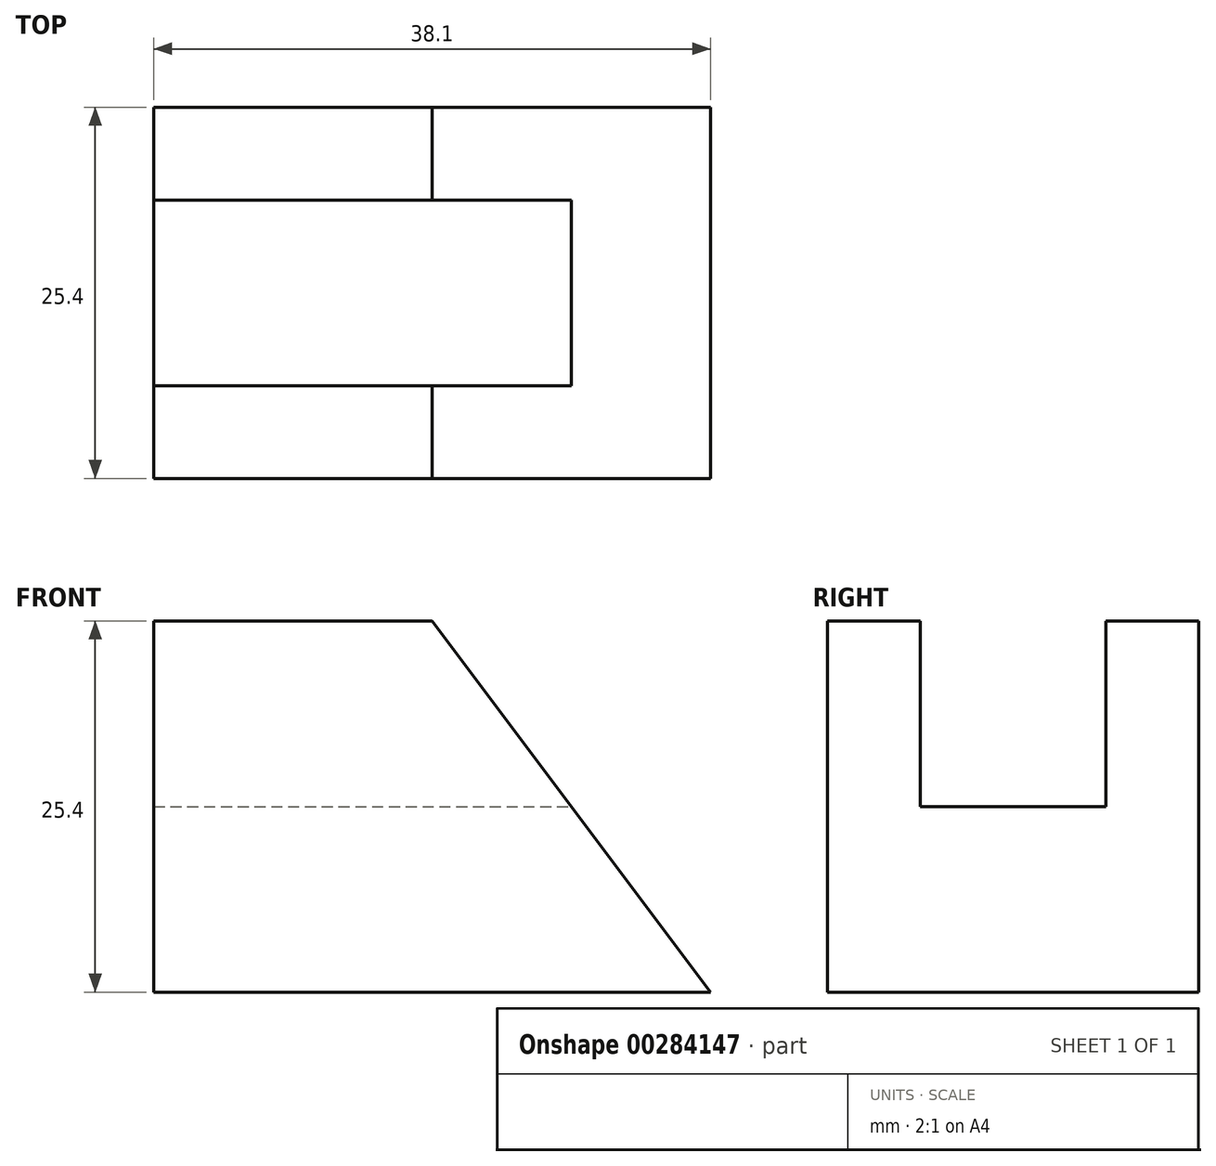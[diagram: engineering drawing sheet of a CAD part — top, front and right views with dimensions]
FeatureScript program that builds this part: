
annotation { "Feature Type Name" : "Feature", "Feature Type Description" : "" }
export const myFeature = defineFeature(function(context is Context, id is Id, definition is map)
    precondition{}
    {
        {
            var Q0;
            Q0=qCreatedBy(makeId("Front.planeOp"),FACE);
            var sketch = newSketch(context, id + "F0", { "sketchPlane" : qUnion([Q0])});
            skLineSegment(sketch, "E0.top", {"start": v(19.05, -12.7) * mm, "end": v(-19.05, -12.7) * mm});
            skLineSegment(sketch, "E0.right", {"start": v(-19.05, 12.7) * mm, "end": v(-19.05, -12.7) * mm});
            skPoint(sketch, "E0.middle", {"position": v(0, 0) * mm});
            skLineSegment(sketch, "E1", {"start": v(-19.05, 12.7) * mm, "end": v(0, 12.7) * mm});
            skLineSegment(sketch, "E2", {"start": v(0, 12.7) * mm, "end": v(19.05, -12.7) * mm});
            skSolve(sketch);
        }
        {
            var Q0;
            Q0=makeQuery(id+"F0.imprint","IMPRINT",FACE,{"disambiguationData":[TD([[makeQuery(id+"F0.imprint","IMPRINT",EDGE,{"derivedFrom":sQuery(id+"F0.wireOp",EDGE,"E0.top")}),-1.0]])]});
            extrude(context, id + "F1", {"entities" : qUnion([Q0]), "endBound" : BoundingType.SYMMETRIC, "depth" : 25.4 * mm});
        }
        {
            var Q0;
            Q0=qCreatedBy(makeId("Right.planeOp"),FACE);
            var sketch = newSketch(context, id + "F2", { "sketchPlane" : qUnion([Q0])});
            skLineSegment(sketch, "E3", {"start": v(-6.35, 0) * mm, "end": v(6.35, 0) * mm});
            skLineSegment(sketch, "E4", {"start": v(6.35, 0) * mm, "end": v(6.35, 12.7) * mm});
            skLineSegment(sketch, "E5", {"start": v(6.35, 12.7) * mm, "end": v(-6.35, 12.7) * mm});
            skLineSegment(sketch, "E6", {"start": v(-6.35, 12.7) * mm, "end": v(-6.35, 0) * mm});
            skSolve(sketch);
        }
        {
            var Q0;
            Q0 = qSketchRegion(id + "F2", true);
            extrude(context, id + "F3", {"entities" : qUnion([Q0]), "operationType" : NewBodyOperationType.REMOVE, "endBound" : BoundingType.THROUGH_ALL, "oppositeDirection" : true, "depth" : 25.4 * mm, "hasSecondDirection" : true, "secondDirectionBound" : SecondDirectionBoundingType.THROUGH_ALL, "secondDirectionOppositeDirection" : false, "secondDirectionDepth" : 25.4 * mm});
        }
    });
